FCSTD DOCUMENT  (FreeCAD 1.1R44227 +568 (Git))
Label: ball_joint
License: All rights reserved
LicenseURL: https://en.wikipedia.org/wiki/All_rights_reserved
objects: Image::ImagePlane×1, App::Point×1, Sketcher::SketchObject×1, PartDesign::Body×1
note: 3 computed .brp shape members not serialized (recipe doc carries the construction recipe); baked Part::Feature solids carry a one-line shape summary decoded from their .brp

FEATURE [Image::ImagePlane] IMG20250629132344
  XSize = 137.01
  YSize = 182.679
FEATURE [App::Point] Origin001
  Role = Origin
FEATURE [Sketcher::SketchObject] Sketch
  ArcFitTolerance = 1e-06
  AttachmentSupport = -> [Origin]
  ExternalTypes = [0]
  FullyConstrained = true
  MakeInternals = false
  MapMode = 5
  _ExternalGeoVersion = 1
  sketch-geometry (10):
    g0: Circle CenterX=-16.68 CenterY=10.16 CenterZ=0 NormalX=0 NormalY=0 NormalZ=1 AngleXU=0 Radius=32.67
    g1: Circle CenterX=-16.68 CenterY=10.16 CenterZ=0 NormalX=0 NormalY=0 NormalZ=1 AngleXU=0 Radius=15.015
    g2: Circle CenterX=6.21 CenterY=23.9 CenterZ=0 NormalX=0 NormalY=0 NormalZ=1 AngleXU=0 Radius=2.97
    g3: Circle CenterX=-40.0242 CenterY=23.1133 CenterZ=0 NormalX=0 NormalY=0 NormalZ=1 AngleXU=0 Radius=2.97
    g4: Circle CenterX=-16.2258 CenterY=-16.5333 CenterZ=0 NormalX=0 NormalY=0 NormalZ=1 AngleXU=0 Radius=2.97
    g5: LineSegment [constr] StartX=-40.0242 StartY=23.1133 StartZ=0 EndX=6.21 EndY=23.9 EndZ=0
    g6: LineSegment [constr] StartX=-16.2258 StartY=-16.5333 StartZ=0 EndX=6.21 EndY=23.9 EndZ=0
    g7: LineSegment [constr] StartX=-16.2258 StartY=-16.5333 StartZ=0 EndX=-40.0242 EndY=23.1133 EndZ=0
    g8: LineSegment [constr] StartX=-16.9071 StartY=23.5067 StartZ=0 EndX=-16.68 EndY=10.16 EndZ=0
    g9: LineSegment [constr] StartX=-5.00791 StartY=3.68334 StartZ=0 EndX=-16.68 EndY=10.16 EndZ=0
  constraints (24):
    c: Coincident(g1,g0)
    c: Diameter(g0) = 65.34
    c: Diameter(g1) = 30.03
    c: DistanceY(g-1,g0) = 10.16
    c: DistanceX(g0,g-1) = 16.68
    c: DistanceX(g0,g2) = 22.89
    c: DistanceY(g0,g2) = 13.74
    c: Coincident(g5,g3)
    c: Coincident(g5,g2)
    c: Coincident(g6,g4)
    c: Coincident(g6,g2)
    c: Coincident(g7,g4)
    c: Coincident(g7,g3)
    c: Equal(g6,g5)
    c: Equal(g5,g7)
    c: Symmetric(g5,g5,g8)
    c: Coincident(g8,g0)
    c: Symmetric(g6,g6,g9)
    c: Coincident(g9,g0)
    c: Perpendicular(g6,g9)
    c: Perpendicular(g5,g8)
    c: Diameter(g2) = 5.94
    c: Equal(g3,g4)
    c: Equal(g4,g2)
FEATURE [PartDesign::Body] Body
  AllowCompound = true
  Group = -> [Sketch]
  Origin = -> Origin
